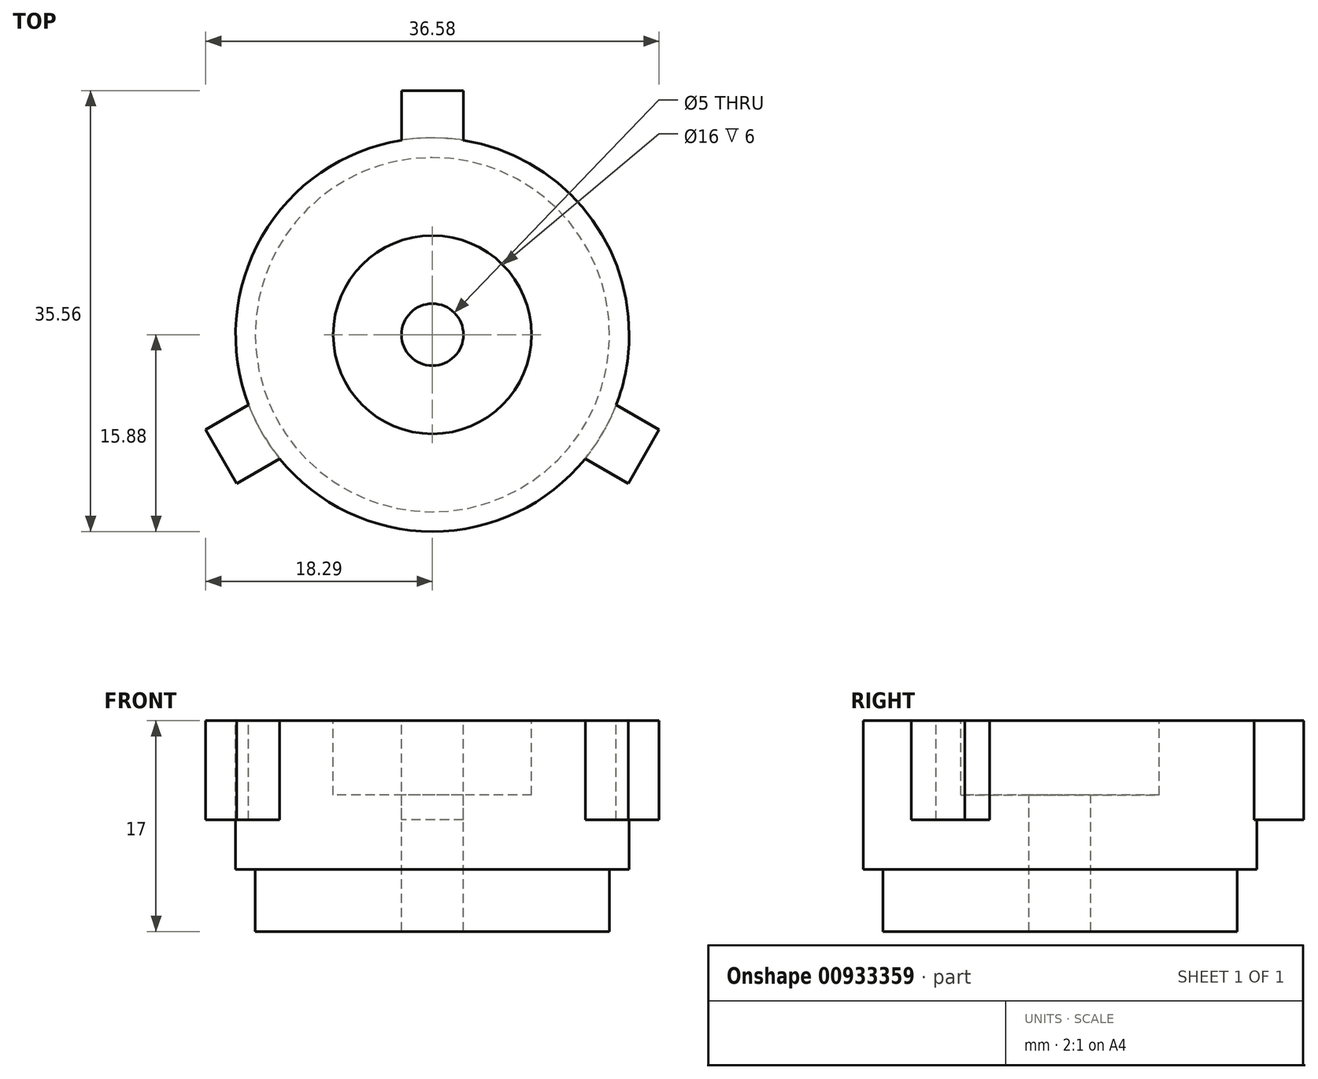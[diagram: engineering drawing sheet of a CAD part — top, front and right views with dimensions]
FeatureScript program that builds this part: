
annotation { "Feature Type Name" : "Feature", "Feature Type Description" : "" }
export const myFeature = defineFeature(function(context is Context, id is Id, definition is map)
    precondition{}
    {
        {
            var Q0;
            Q0=qCreatedBy(makeId("Front.planeOp"),FACE);
            var sketch = newSketch(context, id + "F0", { "sketchPlane" : qUnion([Q0])});
            skLineSegment(sketch, "E0", {"start": v(0, 0) * mm, "end": v(0, -17) * mm});
            skLineSegment(sketch, "E1", {"start": v(0, -17) * mm, "end": v(-14.29, -17) * mm});
            skLineSegment(sketch, "E2", {"start": v(-14.29, -17) * mm, "end": v(-14.29, -12) * mm});
            skLineSegment(sketch, "E3", {"start": v(-14.29, -12) * mm, "end": v(-14.29, -12) * mm});
            skLineSegment(sketch, "E4", {"start": v(-15.87, -12) * mm, "end": v(-14.29, -12) * mm});
            skLineSegment(sketch, "E5", {"start": v(-15.88, -12) * mm, "end": v(-15.88, 0) * mm});
            skLineSegment(sketch, "E6", {"start": v(-15.88, 0) * mm, "end": v(-15.88, 0) * mm});
            skLineSegment(sketch, "E7", {"start": v(-15.88, 0) * mm, "end": v(0, 0) * mm});
            skLineSegment(sketch, "E8", {"start": v(0, -17) * mm, "end": v(0, -29.23) * mm, "construction": true});
            skSolve(sketch);
        }
        {
            var Q0;
            Q0=makeQuery(id+"F0.imprint","IMPRINT",FACE,{"disambiguationData":[TD([[makeQuery(id+"F0.imprint","IMPRINT",EDGE,{"derivedFrom":sQuery(id+"F0.wireOp",EDGE,"E0")}),-1.0]])]});
            var Q1;
            Q1=sQuery(id+"F0.wireOp",EDGE,"E8");
            revolve(context, id + "F1", {"surfaceOperationType" : NewSurfaceOperationType.NEW, "entities" : qUnion([Q0]), "axis" : qUnion([Q1]), "revolveType" : RevolveType.FULL});
        }
        {
            var Q0;
            Q0=makeQuery(id+"F1.opRevolve","SWEPT_FACE",FACE,{"disambiguationData":[OSD([sQuery(id+"F0.wireOp",EDGE,"E7")])]});
            var sketch = newSketch(context, id + "F2", { "sketchPlane" : qUnion([Q0])});
            skPoint(sketch, "E9", {"position": v(0, 0) * mm});
            skSolve(sketch);
        }
        {
            var Q0;
            Q0=sQuery(id+"F2.wireOp",VERTEX,"E9");
            var Q1;
            Q1=makeQuery(id+"F1.opRevolve","SWEPT_BODY",BODY,{"disambiguationData":[OSD([sQuery(id+"F0.wireOp",EDGE,"E0"),sQuery(id+"F0.wireOp",EDGE,"E1"),sQuery(id+"F0.wireOp",EDGE,"E2"),sQuery(id+"F0.wireOp",EDGE,"E4"),sQuery(id+"F0.wireOp",EDGE,"E5"),sQuery(id+"F0.wireOp",EDGE,"E7")])]});
            hole(context, id + "F3", {"style" : HoleStyle.C_BORE, "endStyle" : HoleEndStyle.THROUGH, "holeDiameter" : 5 * mm, "cBoreDiameter" : 16 * mm, "cBoreDepth" : 6 * mm, "majorDiameter" : 5 * mm, "isTappedThrough" : true, "tappedDepth" : 12 * mm, "tapClearance" : 3, "locations" : qUnion([Q0]), "scope" : qUnion([Q1])});
        }
        {
            var Q0;
            Q0=makeQuery(id+"F1.opRevolve","SWEPT_FACE",FACE,{"disambiguationData":[OSD([sQuery(id+"F0.wireOp",EDGE,"E7")])]});
            var sketch = newSketch(context, id + "F4", { "sketchPlane" : qUnion([Q0])});
            skLineSegment(sketch, "E10.bottom", {"start": v(2.5, 15.68) * mm, "end": v(-2.5, 15.68) * mm});
            skLineSegment(sketch, "E10.top", {"start": v(2.5, 19.68) * mm, "end": v(-2.5, 19.68) * mm});
            skLineSegment(sketch, "E10.left", {"start": v(2.5, 15.68) * mm, "end": v(2.5, 19.68) * mm});
            skLineSegment(sketch, "E10.right", {"start": v(-2.5, 15.68) * mm, "end": v(-2.5, 19.68) * mm});
            skPoint(sketch, "E10.middle", {"position": v(0, 17.68) * mm});
            skSolve(sketch);
        }
        {
            var Q0;
            Q0 = qSketchRegion(id + "F4", true);
            extrude(context, id + "F5", {"entities" : qUnion([Q0]), "operationType" : NewBodyOperationType.ADD, "oppositeDirection" : true, "depth" : 8 * mm, "offsetDistance" : 25 * mm});
        }
        {
            var Q0;
            Q0=makeQuery(id+"F1.opRevolve","SWEPT_BODY",BODY,{"disambiguationData":[OSD([sQuery(id+"F0.wireOp",EDGE,"E0"),sQuery(id+"F0.wireOp",EDGE,"E1"),sQuery(id+"F0.wireOp",EDGE,"E2"),sQuery(id+"F0.wireOp",EDGE,"E4"),sQuery(id+"F0.wireOp",EDGE,"E5"),sQuery(id+"F0.wireOp",EDGE,"E7")])]});
            var Q1;
            Q1=makeQuery(id+"F1.opRevolve","SWEPT_FACE",FACE,{"disambiguationData":[OSD([sQuery(id+"F0.wireOp",EDGE,"E2")])]});
            circularPattern(context, id + "F6", {"operationType" : NewBodyOperationType.ADD, "entities" : qUnion([Q0]), "axis" : qUnion([Q1]), "angle" : 360 * degree, "instanceCount" : 3, "equalSpace" : true});
        }
    });
